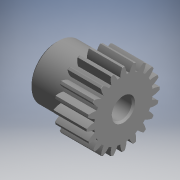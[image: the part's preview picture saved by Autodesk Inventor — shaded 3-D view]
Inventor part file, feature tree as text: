
AUTODESK INVENTOR PART (.ipt)
format: ipt  version: 2017.3 (Build 213256000, 256)  size: 285,184 bytes
history: native  units: mm (DEFAULTED — no unit token found)
features: sketch x2, revolve x1, extrude x1
ambient origin geometry x8: Origin, YZ Plane, XZ Plane, XY Plane, X Axis, Y Axis, Z Axis, Center Point
bodies: Solid1 (feature_tree)
feature tree (4):
  revolve  "Revolution1"  [1 undecoded]
  extrude  "Extrusion1"  [1 undecoded]
  sketch  "Sketch_8"  dims[d0=360.0deg d1=10.0mm d2=0.0mm]
  sketch  "Sketch_11"
note: 2 required parameter values undecoded (feature->parameter linkage not recoverable at this tier; creation-order binding heuristic only, values carry confidence <= 0.55)